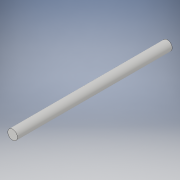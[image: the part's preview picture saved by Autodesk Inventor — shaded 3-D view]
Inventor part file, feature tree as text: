
AUTODESK INVENTOR PART (.ipt)
format: ipt  version: 2019 (Build 230136000, 136)  size: 90,112 bytes
history: native  units: in
note: dims shown in document units (in); Inventor stores cm internally (conversion verified against a paired STEP export)
features: extrude x1, sketch x1
ambient origin geometry x8: Origin, YZ Plane, XZ Plane, XY Plane, X Axis, Y Axis, Z Axis, Center Point
bodies: Solid1 (feature_tree)
feature tree (2):
  extrude  "Extrusion1"  Depth=4.0in TaperAngle=0.0deg
  sketch  "Sketch1"  dims[d0=0.25in d1=4.0in d2=0.0in]
